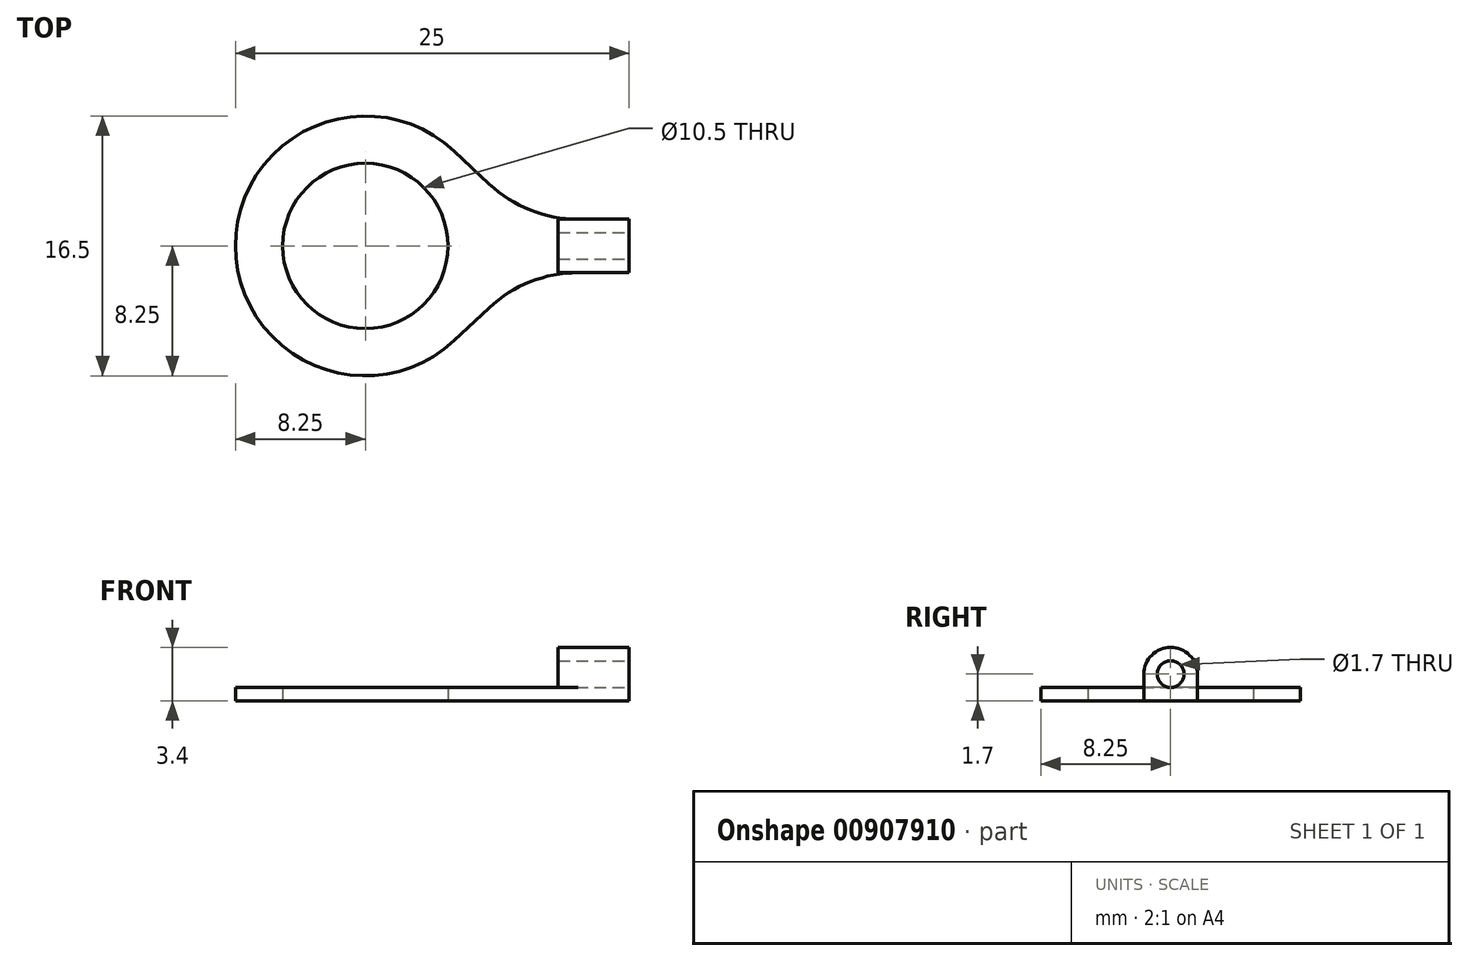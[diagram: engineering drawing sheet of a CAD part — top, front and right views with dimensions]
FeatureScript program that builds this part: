
annotation { "Feature Type Name" : "Feature", "Feature Type Description" : "" }
export const myFeature = defineFeature(function(context is Context, id is Id, definition is map)
    precondition{}
    {
        {
            var Q0;
            Q0=qCreatedBy(makeId("Top.planeOp"),FACE);
            var sketch = newSketch(context, id + "F0", { "sketchPlane" : qUnion([Q0])});
            skLineSegment(sketch, "E0.left", {"start": v(0, 8.25) * mm, "end": v(0, 8.25) * mm});
            skLineSegment(sketch, "E0.right", {"start": v(25, 6.55) * mm, "end": v(25, 9.95) * mm});
            skPoint(sketch, "E1.visualSharp", {"position": v(0, 16.5) * mm});
            skArc(sketch, "E1.filletArc", {"start": v(8.25, 16.5) * mm, "mid": v(2.42, 14.08) * mm, "end": v(0, 8.25) * mm});
            skPoint(sketch, "E2.visualSharp", {"position": v(0, 0) * mm});
            skArc(sketch, "E2.filletArc", {"start": v(0, 8.25) * mm, "mid": v(2.42, 2.42) * mm, "end": v(8.25, 0) * mm});
            skArc(sketch, "E3", {"start": v(13.9, 14.27) * mm, "mid": v(0, 8.25) * mm, "end": v(13.9, 2.23) * mm});
            skCircle(sketch, "E4", {"center": v(8.25, 8.25) * mm, "radius": 5.25 * mm});
            skLineSegment(sketch, "E5.bottom", {"start": v(25, 6.55) * mm, "end": v(21.76, 6.55) * mm});
            skLineSegment(sketch, "E5.top", {"start": v(25, 9.95) * mm, "end": v(21.76, 9.95) * mm});
            skPoint(sketch, "E5.middle", {"position": v(25, 8.25) * mm});
            skLineSegment(sketch, "E6", {"start": v(16.12, 12.18) * mm, "end": v(13.9, 14.27) * mm});
            skLineSegment(sketch, "E7", {"start": v(16.12, 4.32) * mm, "end": v(13.9, 2.23) * mm});
            skPoint(sketch, "E8.visualSharp", {"position": v(18.5, 9.95) * mm});
            skArc(sketch, "E8.filletArc", {"start": v(16.12, 12.18) * mm, "mid": v(18.73, 10.53) * mm, "end": v(21.76, 9.95) * mm});
            skPoint(sketch, "E9.visualSharp", {"position": v(18.5, 6.55) * mm});
            skArc(sketch, "E9.filletArc", {"start": v(21.76, 6.55) * mm, "mid": v(18.73, 5.97) * mm, "end": v(16.12, 4.32) * mm});
            skPoint(sketch, "E10.orphan", {"position": v(29.5, 9.95) * mm});
            skPoint(sketch, "E11.orphan", {"position": v(29.5, 6.55) * mm});
            skPoint(sketch, "E0.top.end.orphan", {"position": v(25, 16.5) * mm});
            skPoint(sketch, "E0.bottom.end.orphan", {"position": v(25, 0) * mm});
            skPoint(sketch, "E5.right.end.orphan", {"position": v(20.5, 9.95) * mm});
            skPoint(sketch, "E5.right.start.orphan", {"position": v(20.5, 6.55) * mm});
            skSolve(sketch);
        }
        {
            var Q0;
            Q0=makeQuery(id+"F0.imprint","IMPRINT",FACE,{"disambiguationData":[TD([[makeQuery(id+"F0.imprint","IMPRINT",EDGE,{"derivedFrom":sQuery(id+"F0.wireOp",EDGE,"E0.right")}),1.0]])]});
            extrude(context, id + "F1", {"entities" : qUnion([Q0]), "depth" : 0.85 * mm, "offsetDistance" : 25 * mm});
        }
        {
            var Q0;
            Q0=makeQuery(id+"F1.opExtrude","CAP_FACE",FACE,{"disambiguationData":[OSD([sQuery(id+"F0.wireOp",EDGE,"E0.right"),sQuery(id+"F0.wireOp",EDGE,"E3"),sQuery(id+"F0.wireOp",EDGE,"E4"),sQuery(id+"F0.wireOp",EDGE,"E5.bottom"),sQuery(id+"F0.wireOp",EDGE,"E5.top"),sQuery(id+"F0.wireOp",EDGE,"E6"),sQuery(id+"F0.wireOp",EDGE,"E7"),sQuery(id+"F0.wireOp",EDGE,"E8.filletArc"),sQuery(id+"F0.wireOp",EDGE,"E9.filletArc")])],"isStart":false});
            var sketch = newSketch(context, id + "F2", { "sketchPlane" : qUnion([Q0])});
            skLineSegment(sketch, "E12.bottom", {"start": v(25, 9.95) * mm, "end": v(20.5, 9.95) * mm});
            skLineSegment(sketch, "E12.top", {"start": v(25, 6.55) * mm, "end": v(20.5, 6.55) * mm});
            skLineSegment(sketch, "E12.left", {"start": v(25, 9.95) * mm, "end": v(25, 6.55) * mm});
            skLineSegment(sketch, "E12.right", {"start": v(20.5, 9.95) * mm, "end": v(20.5, 6.55) * mm});
            skSolve(sketch);
        }
        {
            var Q0;
            {var subQ3=sQuery(id+"F2.wireOp",EDGE,"E12.left");Q0=makeQuery(id+"F2.imprint","IMPRINT",FACE,{"disambiguationData":[TD([[makeQuery(id+"F2.imprint","IMPRINT",EDGE,{"derivedFrom":subQ3}),1.0]])]});}
            extrude(context, id + "F3", {"entities" : qUnion([Q0]), "operationType" : NewBodyOperationType.ADD, "depth" : 2.55 * mm, "offsetDistance" : 25 * mm});
        }
        {
            var Q0;
            Q0=makeQuery(id+"F3.opExtrude","CAP_EDGE",EDGE,{"disambiguationData":[OSD([sQuery(id+"F2.wireOp",EDGE,"E12.bottom")])],"isStart":false});
            var Q1;
            Q1=makeQuery(id+"F3.opExtrude","CAP_EDGE",EDGE,{"disambiguationData":[OSD([sQuery(id+"F2.wireOp",EDGE,"E12.top")])],"isStart":false});
            fillet(context, id + "F4", {"entities" : qUnion([Q0, Q1]), "radius" : 1.7 * mm, "tangentPropagation" : true, "allowEdgeOverflow" : false});
        }
        {
            var Q0;
            Q0=makeQuery(id+"F3.boolean.opBoolean","MERGE",FACE,{"derivedFrom":[makeQuery(id+"F1.opExtrude","SWEPT_FACE",FACE,{"disambiguationData":[OSD([sQuery(id+"F0.wireOp",EDGE,"E0.right")])]}),makeQuery(id+"F3.opExtrude","SWEPT_FACE",FACE,{"disambiguationData":[OSD([sQuery(id+"F2.wireOp",EDGE,"E12.left")])]})]});
            var sketch = newSketch(context, id + "F5", { "sketchPlane" : qUnion([Q0])});
            skCircle(sketch, "E13", {"center": v(8.25, 1.7) * mm, "radius": 0.85 * mm});
            skSolve(sketch);
        }
        {
            var Q0;
            Q0 = qSketchRegion(id + "F5", true);
            extrude(context, id + "F6", {"entities" : qUnion([Q0]), "operationType" : NewBodyOperationType.REMOVE, "oppositeDirection" : true, "depth" : 25 * mm, "offsetDistance" : 25 * mm});
        }
    });
